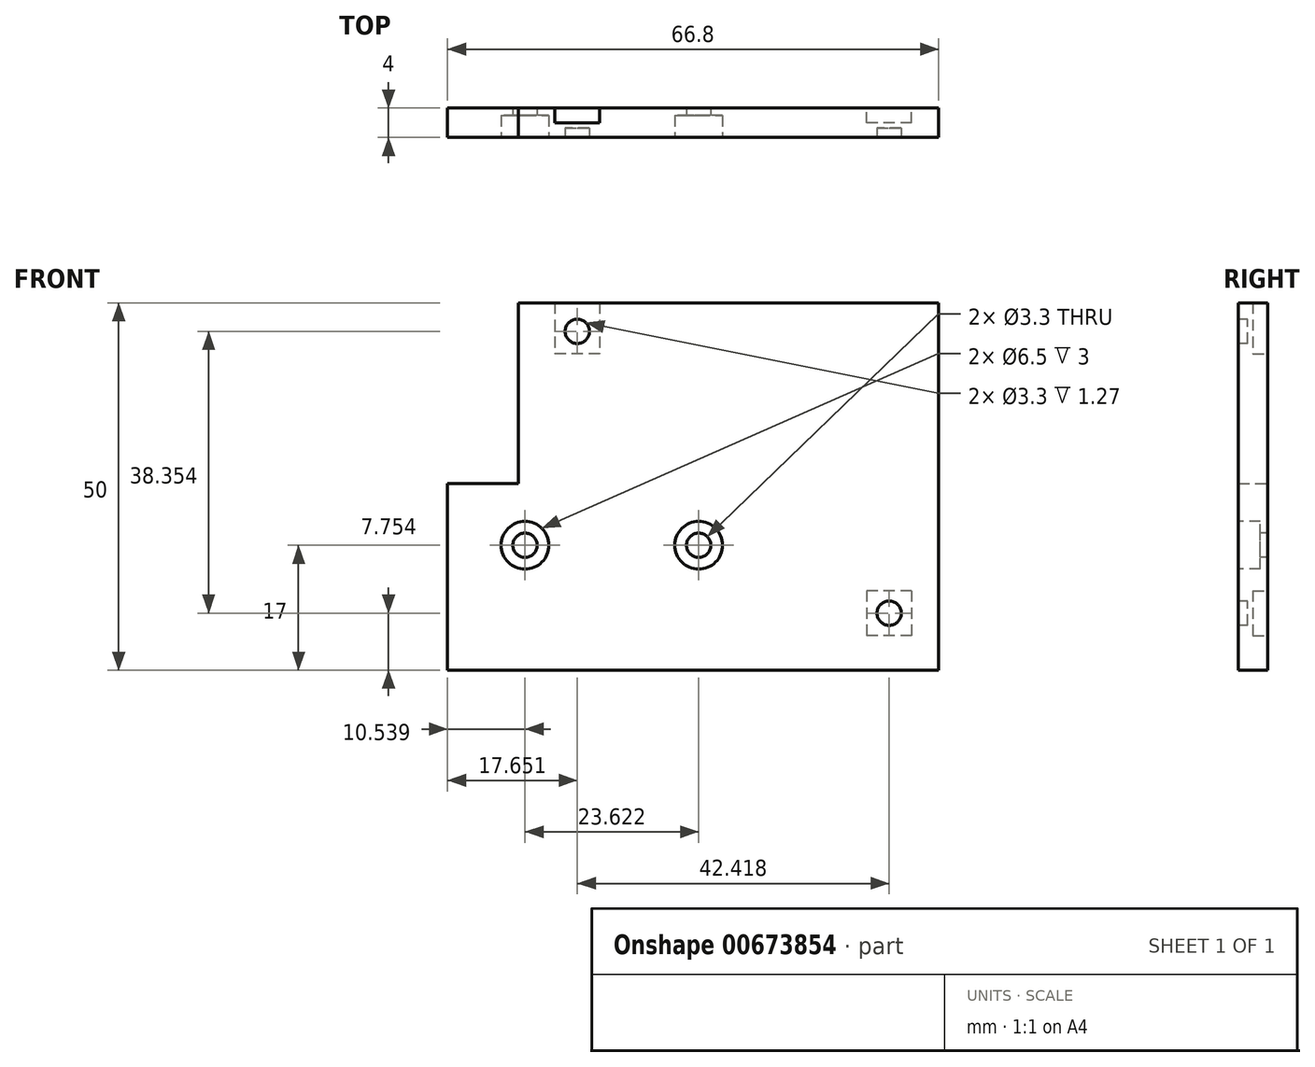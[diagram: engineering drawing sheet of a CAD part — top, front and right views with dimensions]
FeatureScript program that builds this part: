
annotation { "Feature Type Name" : "Feature", "Feature Type Description" : "" }
export const myFeature = defineFeature(function(context is Context, id is Id, definition is map)
    precondition{}
    {
        {
            var Q0;
            Q0=qCreatedBy(makeId("Front.planeOp"),FACE);
            var sketch = newSketch(context, id + "F0", { "sketchPlane" : qUnion([Q0])});
            skLineSegment(sketch, "E0.bottom", {"start": v(-12.7, 74) * mm, "end": v(44.45, 74) * mm});
            skLineSegment(sketch, "E0.top", {"start": v(-22.35, 24) * mm, "end": v(44.45, 24) * mm});
            skLineSegment(sketch, "E1", {"start": v(44.45, 24) * mm, "end": v(44.45, 74) * mm});
            skLineSegment(sketch, "E2", {"start": v(-22.35, 24) * mm, "end": v(-22.35, 49.4) * mm});
            skLineSegment(sketch, "E3", {"start": v(-22.35, 49.4) * mm, "end": v(-12.7, 49.4) * mm});
            skLineSegment(sketch, "E4", {"start": v(-12.7, 49.4) * mm, "end": v(-12.7, 74) * mm});
            skSolve(sketch);
        }
        {
            var Q0;
            Q0 = qSketchRegion(id + "F0", true);
            extrude(context, id + "F1", {"entities" : qUnion([Q0]), "depth" : 4 * mm, "offsetDistance" : 25.4 * mm});
        }
        {
            var Q0;
            Q0=makeQuery(id+"F1.opExtrude","CAP_FACE",FACE,{"disambiguationData":[OSD([sQuery(id+"F0.wireOp",EDGE,"E0.bottom"),sQuery(id+"F0.wireOp",EDGE,"E0.top"),sQuery(id+"F0.wireOp",EDGE,"E0.left"),sQuery(id+"F0.wireOp",EDGE,"E0.right")])],"isStart":false});
            var sketch = newSketch(context, id + "F2", { "sketchPlane" : qUnion([Q0])});
            skPoint(sketch, "E5", {"position": v(-11.81, 41) * mm});
            skPoint(sketch, "E6", {"position": v(11.81, 41) * mm});
            skLineSegment(sketch, "E7", {"start": v(-11.81, 41) * mm, "end": v(11.81, 41) * mm, "construction": true});
            skSolve(sketch);
        }
        {
            var Q0;
            Q0=sQuery(id+"F2.wireOp",VERTEX,"E5");
            var Q1;
            Q1=sQuery(id+"F2.wireOp",VERTEX,"E6");
            var Q2;
            Q2=makeQuery(id+"F1.opExtrude","SWEPT_BODY",BODY,{"disambiguationData":[OSD([sQuery(id+"F0.wireOp",EDGE,"E0.bottom"),sQuery(id+"F0.wireOp",EDGE,"E0.top"),sQuery(id+"F0.wireOp",EDGE,"E0.left"),sQuery(id+"F0.wireOp",EDGE,"E0.right")])]});
            hole(context, id + "F3", {"style" : HoleStyle.C_BORE, "endStyle" : HoleEndStyle.THROUGH, "standardTappedOrClearance" : lookupTablePath({ "standard" : "ISO", "fit" : "Normal", "size" : "M3", "type" : "Clearance" }), "standardBlindInLast" : lookupTablePath({ "fit" : "Standard", "standard" : "ISO", "size" : "M3", "type" : "Clearance" }), "holeDiameter" : 3.3 * mm, "cBoreDiameter" : 6.5 * mm, "cBoreDepth" : 3 * mm, "majorDiameter" : 6.35 * mm, "isTappedThrough" : true, "tappedDepth" : 50.8 * mm, "tapClearance" : 3, "locations" : qUnion([Q0, Q1]), "scope" : qUnion([Q2])});
        }
        {
            var Q0;
            Q0=makeQuery(id+"F1.opExtrude","CAP_FACE",FACE,{"disambiguationData":[OSD([sQuery(id+"F0.wireOp",EDGE,"E0.bottom"),sQuery(id+"F0.wireOp",EDGE,"E0.top"),sQuery(id+"F0.wireOp",EDGE,"E0.left"),sQuery(id+"F0.wireOp",EDGE,"E1"),sQuery(id+"F0.wireOp",EDGE,"qHf1nInt-oGBS-weHY-rNIp-B3Kh8PWKOxkt"),sQuery(id+"F0.wireOp",EDGE,"U1nYR2As-foFV-aHNI-jMxd-9pyeD7hILSAe")])],"isStart":false});
            var sketch = newSketch(context, id + "F4", { "sketchPlane" : qUnion([Q0])});
            skPoint(sketch, "E8", {"position": v(-4.7, 70.1) * mm});
            skPoint(sketch, "E9", {"position": v(37.72, 31.75) * mm});
            skLineSegment(sketch, "E10", {"start": v(37.72, 31.75) * mm, "end": v(-4.7, 31.75) * mm, "construction": true});
            skLineSegment(sketch, "E11", {"start": v(-4.7, 31.75) * mm, "end": v(-4.7, 70.1) * mm, "construction": true});
            skCircle(sketch, "E12", {"center": v(37.72, 31.75) * mm, "radius": 1.65 * mm});
            skCircle(sketch, "E13", {"center": v(-4.7, 70.1) * mm, "radius": 1.65 * mm});
            skSolve(sketch);
        }
        {
            var Q0;
            Q0=makeQuery(id+"F1.opExtrude","CAP_FACE",FACE,{"disambiguationData":[OSD([sQuery(id+"F0.wireOp",EDGE,"E0.bottom"),sQuery(id+"F0.wireOp",EDGE,"E0.top"),sQuery(id+"F0.wireOp",EDGE,"E0.left"),sQuery(id+"F0.wireOp",EDGE,"E1"),sQuery(id+"F0.wireOp",EDGE,"qHf1nInt-oGBS-weHY-rNIp-B3Kh8PWKOxkt"),sQuery(id+"F0.wireOp",EDGE,"U1nYR2As-foFV-aHNI-jMxd-9pyeD7hILSAe")])],"isStart":true});
            var sketch = newSketch(context, id + "F5", { "sketchPlane" : qUnion([Q0])});
            skLineSegment(sketch, "E14.bottom", {"start": v(1.65, 82.18) * mm, "end": v(7.75, 82.18) * mm});
            skLineSegment(sketch, "E14.top", {"start": v(1.65, 67.06) * mm, "end": v(7.75, 67.06) * mm});
            skLineSegment(sketch, "E14.left", {"start": v(1.65, 82.18) * mm, "end": v(1.65, 67.06) * mm});
            skLineSegment(sketch, "E14.right", {"start": v(7.75, 82.18) * mm, "end": v(7.75, 67.06) * mm});
            skLineSegment(sketch, "E15.bottom", {"start": v(-40.77, 34.8) * mm, "end": v(-34.67, 34.8) * mm});
            skLineSegment(sketch, "E15.top", {"start": v(-40.77, 28.7) * mm, "end": v(-34.67, 28.7) * mm});
            skLineSegment(sketch, "E15.left", {"start": v(-34.67, 34.8) * mm, "end": v(-34.67, 28.7) * mm});
            skLineSegment(sketch, "E15.right", {"start": v(-40.77, 34.8) * mm, "end": v(-40.77, 28.7) * mm});
            skSolve(sketch);
        }
        {
            var Q0;
            Q0 = qSketchRegion(id + "F5", true);
            extrude(context, id + "F6", {"entities" : qUnion([Q0]), "operationType" : NewBodyOperationType.REMOVE, "oppositeDirection" : true, "depth" : 2.03 * mm, "offsetDistance" : 25.4 * mm});
        }
        {
            var Q0;
            Q0 = qSketchRegion(id + "F4", true);
            extrude(context, id + "F7", {"entities" : qUnion([Q0]), "operationType" : NewBodyOperationType.REMOVE, "oppositeDirection" : true, "depth" : 1.27 * mm, "offsetDistance" : 25.4 * mm});
        }
    });
